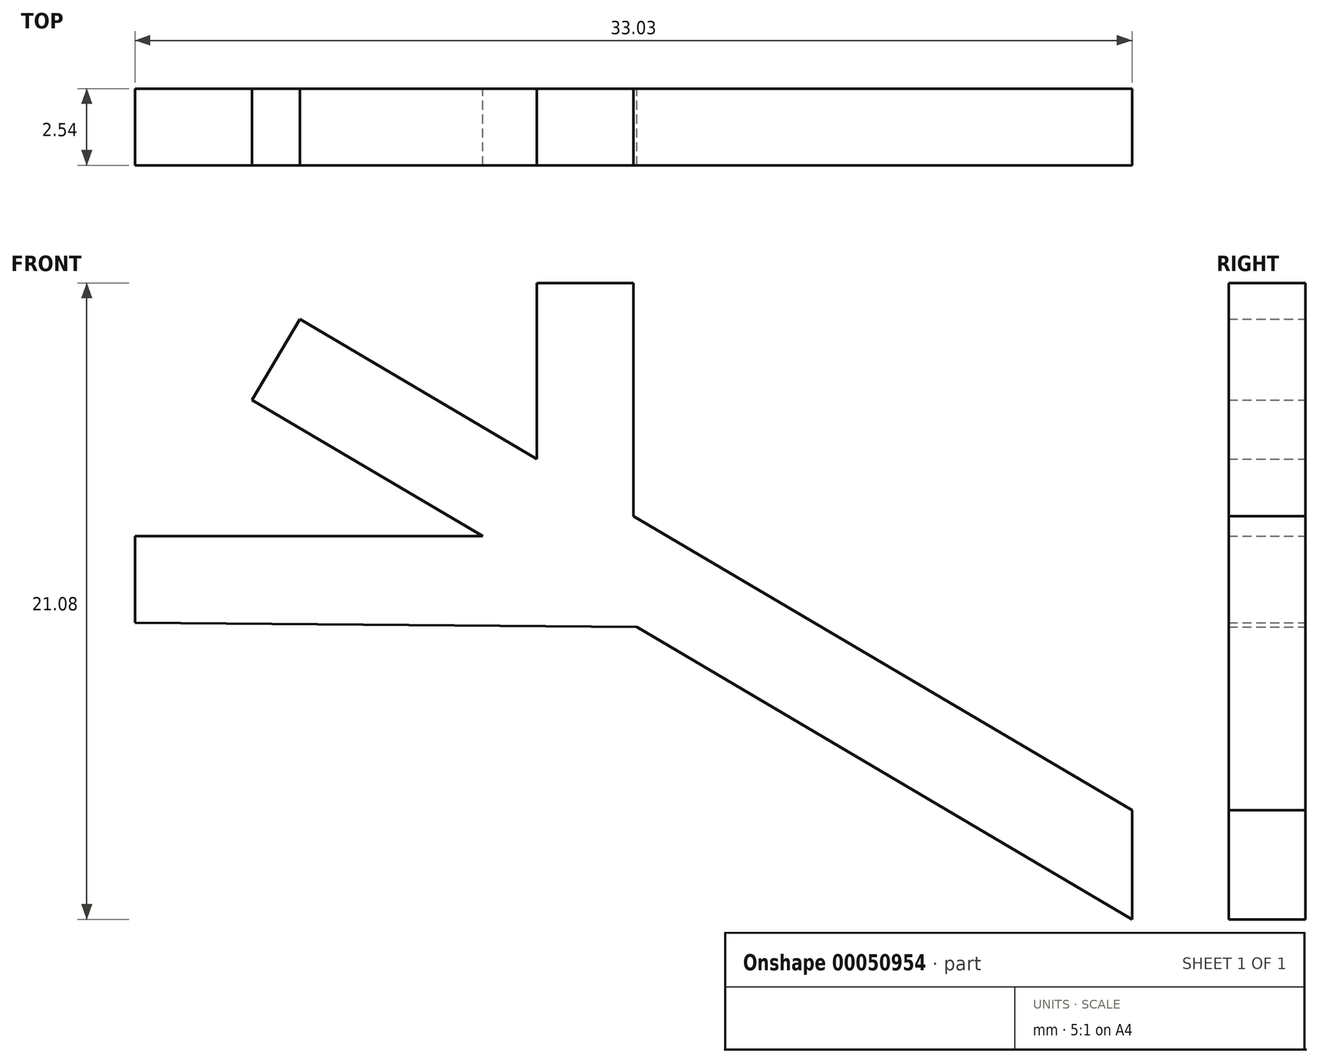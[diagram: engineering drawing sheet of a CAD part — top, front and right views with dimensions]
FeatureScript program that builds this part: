
annotation { "Feature Type Name" : "Feature", "Feature Type Description" : "" }
export const myFeature = defineFeature(function(context is Context, id is Id, definition is map)
    precondition{}
    {
        {
            var Q0;
            Q0=qCreatedBy(makeId("Front.planeOp"),FACE);
            var sketch = newSketch(context, id + "F0", { "sketchPlane" : qUnion([Q0])});
            skLineSegment(sketch, "E0", {"start": v(0, 0) * mm, "end": v(-16.4, 9.68) * mm});
            skLineSegment(sketch, "E1", {"start": v(-29.15, 17.2) * mm, "end": v(-27.57, 19.88) * mm});
            skLineSegment(sketch, "E2", {"start": v(-27.57, 19.88) * mm, "end": v(-19.72, 15.24) * mm});
            skLineSegment(sketch, "E3", {"start": v(0, 3.61) * mm, "end": v(0, -0.94) * mm});
            skLineSegment(sketch, "E4", {"start": v(-19.72, 15.24) * mm, "end": v(-19.72, 21.08) * mm});
            skLineSegment(sketch, "E5", {"start": v(-19.72, 21.08) * mm, "end": v(-16.52, 21.08) * mm});
            skLineSegment(sketch, "E6", {"start": v(-16.52, 21.08) * mm, "end": v(-16.52, 13.36) * mm});
            skLineSegment(sketch, "E7", {"start": v(-21.5, 12.7) * mm, "end": v(-33.03, 12.7) * mm});
            skLineSegment(sketch, "E8", {"start": v(-33.03, 12.7) * mm, "end": v(-33.03, 9.82) * mm});
            skLineSegment(sketch, "E9", {"start": v(-33.03, 9.82) * mm, "end": v(-16.4, 9.68) * mm});
            skLineSegment(sketch, "E10.trimOffspring", {"start": v(-21.5, 12.7) * mm, "end": v(-29.15, 17.2) * mm});
            skLineSegment(sketch, "E11.trimOffspring", {"start": v(-16.52, 13.36) * mm, "end": v(0, 3.61) * mm});
            skSolve(sketch);
        }
        {
            var Q0;
            {var subQ0=sQuery(id+"F0.wireOp",EDGE,"E0");Q0=makeQuery(id+"F0.imprint","IMPRINT",FACE,{"disambiguationData":[TD([[makeQuery(id+"F0.imprint","IMPRINT",EDGE,{"derivedFrom":subQ0}),-1.0]])]});}
            extrude(context, id + "F1", {"entities" : qUnion([Q0]), "depth" : 2.54 * mm});
        }
    });
